# Revit family: 0047181
name_source: partatom
category: Lighting Fixtures
revit_build: Autodesk Revit 2017 (Build: 20190507_1515(x64)
units: mm (PartAtom-declared; Revit-internal decimal feet)

## family parameters
Cut with Voids When Loaded = No
Host = Face
Light Source = Yes
OmniClass Number = 23.80.70.00
OmniClass Title = Lighting
Part Type = Normal
Room Calculation Point = No
Round Connector Dimension = Use Diameter
Shared = No

## types (1)
- 0047181 ST WTRPRF TUBULAR 1500 IP66 7400 840 PC
    AccessoryMaterial = <By Category>
    Apparent Load = 50 VA
    Assembly Code = D5020200
    AssetType = Fixed
    BodyMaterial = Body-Sylvania-SylproofTubular-Aluminium
    BracketDistance_SYL = 1350 mm  [stored 4.42913 ft]
    BracketWidth_SYL = 25 mm  [stored 0.082021 ft]
    ClassificationName = Uniclass2015
    ClassificationValue = EF_70_80
    Color Filter = 16777215
    Cost = 0 $
    Default Elevation = 1219 mm
    DiffuserMaterial = Diffuser-Sylvania-SylproofTubular-Opal
    Dimming Lamp Color Temperature Shift = <None>
    DimmingControlOptions = Non-dimmable
    DocumentationLiterature = http://www.sylvania-lighting.com
    DurationUnit = hours
    ElectricShockClassification = Class I
    Emit Shape Visible in Rendering = No
    Emit from Rectangle Length = 1480 mm  [stored 4.85564 ft]
    Emit from Rectangle Width = 90 mm  [stored 0.295276 ft]
    ExpectedLife = 50000
    IfcExportAs = IfcLightFixtureType
    IfcExportType = IfcLightFixtureType
    ImpactProtectionIndex = IK10
    IngressProtection = IP66
    InputNominalFrequency = 50/60 Hz
    InputVoltage = 220-240 V AC
    Keynote = 16500
    Lamp = LED
    LampColourRenderingIndex = 80
    LampColourTemperature = 4000 K
    LampNominalLuminous = 7400 lm
    LampsType = LED
    LuminousEfficacy = 148 lm/W
    Manufacturer = Feilo Sylvania
    ManufacturerName = Feilo Sylvania
    Model = START Waterproof Tubular 1500 IP66 7400lm 840 PC
    ModelNumber = 0047181
    ModelReference = START Waterproof Tubular 1500 IP66 7400lm 840 PC
    Name = START Waterproof Tubular 1500 IP66 7400lm 840 PC
    NominalDepth = 70 mm  [stored 0.229659 ft]
    NominalHeight = 70 mm  [stored 0.229659 ft]
    NominalLength = 1495 mm
    Photometric Web File = 0047181.ies
    PowerConsumption = 50 W
    PowerFactor = 0.95
    ReflectorMaterial = Reflector-Sylvania-SylproofTubular-Illumination
    Tilt Angle = -90.00°
    TubeDiameterInside_SYL = 66 mm  [stored 0.216535 ft]
    TubeDiameterOutside_SYL = 70 mm  [stored 0.229659 ft]
    TubeLength_SYL = 1500 mm  [stored 4.92126 ft]
    Type Image = <None>
    TypeName = START Waterproof Tubular 1500 IP66 7400lm 840 PC
    URL = http://www.sylvania-lighting.com
    Voltage = 230 V
    Weight = 6.2 kg

note: [stored X ft] marks values corroborated as IEEE doubles in the binary element streams (Revit-internal decimal feet)

## geometry (parser evidence)
native form markers: Sweep x5
no freeform markers — native parametric forms only
